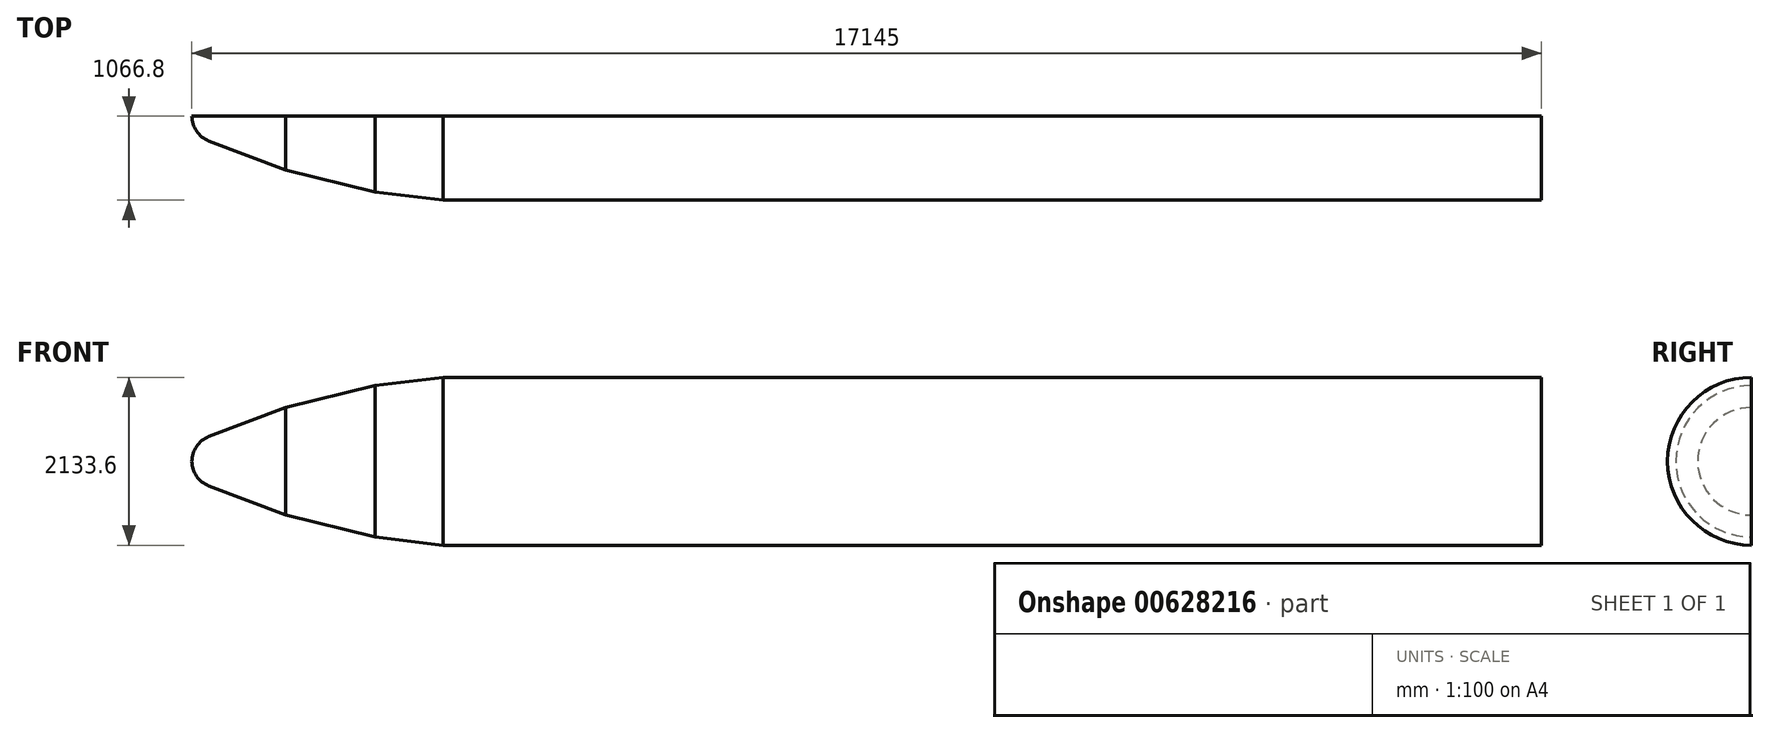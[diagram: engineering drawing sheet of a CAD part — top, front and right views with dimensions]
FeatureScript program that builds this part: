
annotation { "Feature Type Name" : "Feature", "Feature Type Description" : "" }
export const myFeature = defineFeature(function(context is Context, id is Id, definition is map)
    precondition{}
    {
        {
            var Q0;
            Q0=qCreatedBy(makeId("Front.planeOp"),FACE);
            var sketch = newSketch(context, id + "F0", { "sketchPlane" : qUnion([Q0])});
            skLineSegment(sketch, "E0", {"start": v(0, 1066.8) * mm, "end": v(13952.68, 1066.8) * mm});
            skLineSegment(sketch, "E1", {"start": v(13952.68, 1066.8) * mm, "end": v(13952.68, 0) * mm});
            skLineSegment(sketch, "E2", {"start": v(0, 1066.8) * mm, "end": v(-864.84, 961.48) * mm});
            skLineSegment(sketch, "E3", {"start": v(-864.84, 961.48) * mm, "end": v(-2002.23, 683.7) * mm});
            skLineSegment(sketch, "E4", {"start": v(-2002.23, 683.7) * mm, "end": v(-2976.83, 312.64) * mm});
            skArc(sketch, "E5", {"start": v(-2976.83, 312.64) * mm, "mid": v(-3133.23, 189.86) * mm, "end": v(-3192.32, 0) * mm});
            skLineSegment(sketch, "E6", {"start": v(-3192.32, 0) * mm, "end": v(-13419.82, 0) * mm, "construction": true});
            skLineSegment(sketch, "E7", {"start": v(13952.68, 0) * mm, "end": v(42473.68, 0) * mm, "construction": true});
            skEllipticalArc(sketch, "E8", {"construction": true});
            skLineSegment(sketch, "E9", {"start": v(42473.68, 0) * mm, "end": v(42473.68, 40933.28) * mm, "construction": true});
            skLineSegment(sketch, "E10", {"start": v(-3192.32, 0) * mm, "end": v(-2738.35, 0) * mm, "construction": true});
            skLineSegment(sketch, "E11", {"start": v(13952.68, 0) * mm, "end": v(-3192.32, 0) * mm});
            const initialGuessF0  = {"E8": [58.36481475830078, 0, -1, 0, 71.78463594053545, 41.97470340448322, 4.935610526474175, 0]};
            skSetInitialGuess(sketch, initialGuessF0);
            skSolve(sketch);
        }
        {
            var Q0;
            Q0 = qSketchRegion(id + "F0", true);
            var Q1;
            Q1=sQuery(id+"F0.wireOp",EDGE,"E7");
            revolve(context, id + "F1", {"entities" : qUnion([Q0]), "axis" : qUnion([Q1]), "revolveType" : RevolveType.ONE_DIRECTION, "angle" : 180 * degree});
        }
        {
            var Q0;
            Q0=qCreatedBy(makeId("Front.planeOp"),FACE);
            var sketch = newSketch(context, id + "F2", { "sketchPlane" : qUnion([Q0])});
            skPoint(sketch, "E12.0", {"position": v(0, 1066.8) * mm});
            skPoint(sketch, "E13.0", {"position": v(0, -1066.8) * mm});
            skLineSegment(sketch, "E14", {"start": v(-13419.82, 0) * mm, "end": v(-10559.6, 0) * mm, "construction": true});
            skEllipticalArc(sketch, "E15.MirrorCS", {"construction": true});
            skLineSegment(sketch, "E16", {"start": v(0, 1066.8) * mm, "end": v(-7685.95, 16438.43) * mm});
            skPoint(sketch, "E17.0", {"position": v(13952.68, 1066.8) * mm});
            skPoint(sketch, "E18.0", {"position": v(13952.68, -1066.8) * mm});
            skEllipticalArc(sketch, "E19.0", {"construction": true});
            skLineSegment(sketch, "E20", {"start": v(13952.68, 1066.8) * mm, "end": v(19112.98, 35143.88) * mm});
            skPoint(sketch, "E21.0", {"position": v(-2976.83, 312.64) * mm});
            skLineSegment(sketch, "E22", {"start": v(-2976.83, 312.64) * mm, "end": v(-12751.35, 5715) * mm});
            skLineSegment(sketch, "E23.0", {"start": v(42473.68, 40933.28) * mm, "end": v(42473.68, -40933.28) * mm, "construction": true});
            skPoint(sketch, "E24.0", {"position": v(-2002.23, 683.7) * mm});
            skPoint(sketch, "E25.0", {"position": v(-864.84, 961.48) * mm});
            skLineSegment(sketch, "E26", {"start": v(-2002.23, 683.7) * mm, "end": v(-11652.57, 9256.5) * mm});
            skLineSegment(sketch, "E27", {"start": v(-864.84, 961.48) * mm, "end": v(-9954.17, 12884.66) * mm});
            skLineSegment(sketch, "E28", {"start": v(42473.68, 11699.44) * mm, "end": v(13035.12, 724.74) * mm});
            const initialGuessF2  = {"E15.MirrorCS": [58.36481475830078, 0, -1, 0, 71.78463594053545, 41.97470340448322, 5.880786000752525, 0], "E19.0": [58.36481475830078, 0, -1, 0, 71.78463594053545, 41.97470340448322, 4.935610526474175, 5.290926399295396]};
            skSetInitialGuess(sketch, initialGuessF2);
            skSolve(sketch);
        }
    });
